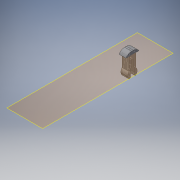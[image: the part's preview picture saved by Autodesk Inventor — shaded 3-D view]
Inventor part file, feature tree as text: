
AUTODESK INVENTOR PART (.ipt)
format: ipt  version: 2017 (Build 210142000, 142)  size: 150,528 bytes
history: native  units: mm
features: extrude x4, sketch x4, other x4, reference x3, fillet x2, plane x1
ambient origin geometry x8: Origin, YZ Plane, XZ Plane, XY Plane, X Axis, Y Axis, Z Axis, Center Point
bodies: Solid1 (feature_tree)
feature tree (18):
  plane  "Work Plane1"
  extrude  "Extrusion1"  Depth=12.0mm TaperAngle=0.0deg
  extrude  "Extrusion2"  Depth=2.0mm TaperAngle=0.0deg
  fillet  "Fillet1"  Radius=4.0mm
  extrude  "Extrusion3"  Depth=3.0mm
  extrude  "Extrusion4"  Depth=4.0mm
  fillet  "Fillet2"  Radius=2.5mm
  sketch  "Sketch1"  dims[d0=45.0deg d1=12.0mm d2=0.0mm]
  reference  "Reference1"
  sketch  "Sketch2"  dims[d3=8.0mm d4=2.0mm d5=0.0mm d6=4.0mm]
  reference  "Reference2"
  sketch  "Sketch3"  dims[d7=3.0mm d8=3.0mm]
  reference  "Reference3"
  sketch  "Sketch4"  dims[d9=2.0mm d10=0.0mm d11=4.0mm d12=2.5mm d13=0.5mm d14=2.0mm d15=0.0mm d16=0.5mm]
  parser-record x1  (decoder bookkeeping rows leaked as tree rows — omitted from the tree; the rows remain in map.json)
  other  "assembly_full.iam"
  other  "top_right:1"
  other  "base:1"
note: 1 file-system path scrubbed to <path> (originals preserved in map.json)
